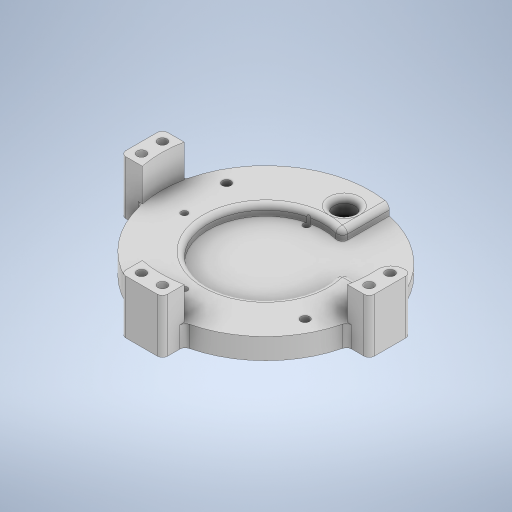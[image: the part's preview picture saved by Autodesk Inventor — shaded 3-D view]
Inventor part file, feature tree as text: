
AUTODESK INVENTOR PART (.ipt)
format: ipt  version: 2023 (Build 270158000, 158)  size: 500,736 bytes
history: native  units: in
note: dims shown in document units (in); Inventor stores cm internally (conversion verified against a paired STEP export)
features: sketch x15, extrude x11, fillet x8, hole x3
ambient origin geometry x8: Origin, YZ Plane, XZ Plane, XY Plane, X Axis, Y Axis, Z Axis, Center Point
bodies: Solid1 (feature_tree)
feature tree (37):
  extrude  "Extrusion1"  Depth=0.2in TaperAngle=0.0deg
  extrude  "Extrusion2"  Depth=0.2in TaperAngle=0.0deg
  extrude  "Extrusion3"  Depth=0.5in
  extrude  "Extrusion4"  Depth=0.4in
  fillet  "Fillet1"  Radius=0.5in
  fillet  "Fillet2"  Radius=0.5in
  fillet  "Fillet3"  Radius=0.4in
  extrude  "Extrusion5"  Depth=0.4in TaperAngle=0.0deg
  extrude  "Extrusion6"  Depth=0.2in
  extrude  "Extrusion8"  Depth=0.2in
  fillet  "Fillet4"  Radius=0.4in
  extrude  "Extrusion9"  Depth=0.2in
  sketch  "Sketch10"  dims[d26=0.4in d30=0.177in]
  hole  "Hole1"  [1 undecoded]
  extrude  "Extrusion10"  Depth=0.177in
  hole  "Hole2"  [1 undecoded]
  fillet  "Fillet5"  Radius=0.1in
  hole  "Hole3"  [1 undecoded]
  extrude  "Extrusion11"  Depth=0.3in TaperAngle=0.0deg
  fillet  "Fillet7"  Radius=0.3in
  extrude  "Extrusion13"  Depth=0.3in
  fillet  "Fillet8"  Radius=0.3in
  fillet  "Fillet9"  Radius=0.3in
  sketch  "Sketch1"  dims[d0=4.0in d1=0.2in d2=0.0in]
  sketch  "Sketch2"  dims[d3=2.2in d4=0.2in d5=0.0in]
  sketch  "Sketch3"  dims[d6=3.75in d10=0.5in]
  sketch  "Sketch4"  dims[d11=0.4in d12=0.4in d13=0.5in d14=0.5in d15=0.4in]
  sketch  "Sketch5"  dims[d16=0.4in d17=1.025in d18=0.0in]
  sketch  "Sketch6"  dims[d19=0.2in d20=0.2in]
  sketch  "Sketch8"  dims[d21=0.4in d22=0.2in d23=0.4in]
  sketch  "Sketch9"  dims[d24=0.2in d25=0.2in]
  sketch  "Sketch11"  dims[d33=0.177in d34=0.177in]
  sketch  "Sketch12"  dims[d35=0.177in d36=5.0in d37=0.0in d38=0.1in]
  sketch  "Sketch13"  dims[d39=0.1in d40=0.1in]
  sketch  "Sketch14"  dims[d41=0.2in d42=0.0in d43=0.625in d44=0.0in d47=0.3in]
  sketch  "Sketch15"  dims[d48=0.3in d49=0.3in d50=0.3in d51=0.3in]
  sketch  "Sketch17"  dims[d52=0.2in d53=0.0in d54=0.1in d55=0.9in d56=0.8875in d57=0.8875in d58=0.25in d59=0.25in d60=0.2in d61=0.0in d62=0.126in d63=0.432in d64=0.256in d65=0.118in d66=90.0deg d67=0.5in d68=0.8108in d69=1.65in d70=45.0deg d71=1.65in d72=45.0deg d73=0.25in d74=0.2in d75=0.0in d76=0.126in d77=0.75in d78=0.375in d79=0.25in d80=0.5635in d81=1.0in d82=0.8108in d83=0.25in d84=0.4154in d85=0.2in d86=1.5in d87=0.75in d88=1.5in d89=0.75in d90=0.169in d91=0.75in d92=0.315in d93=0.157in d94=0.5635in d95=1.0in d96=0.8108in d97=0.6875in d98=0.0in d102=0.1in d103=1.5in d104=0.4in d105=1.0in d106=0.0in d107=0.1in d108=0.1in]
note: 3 required parameter values undecoded (feature->parameter linkage not recoverable at this tier; creation-order binding heuristic only, values carry confidence <= 0.55)
